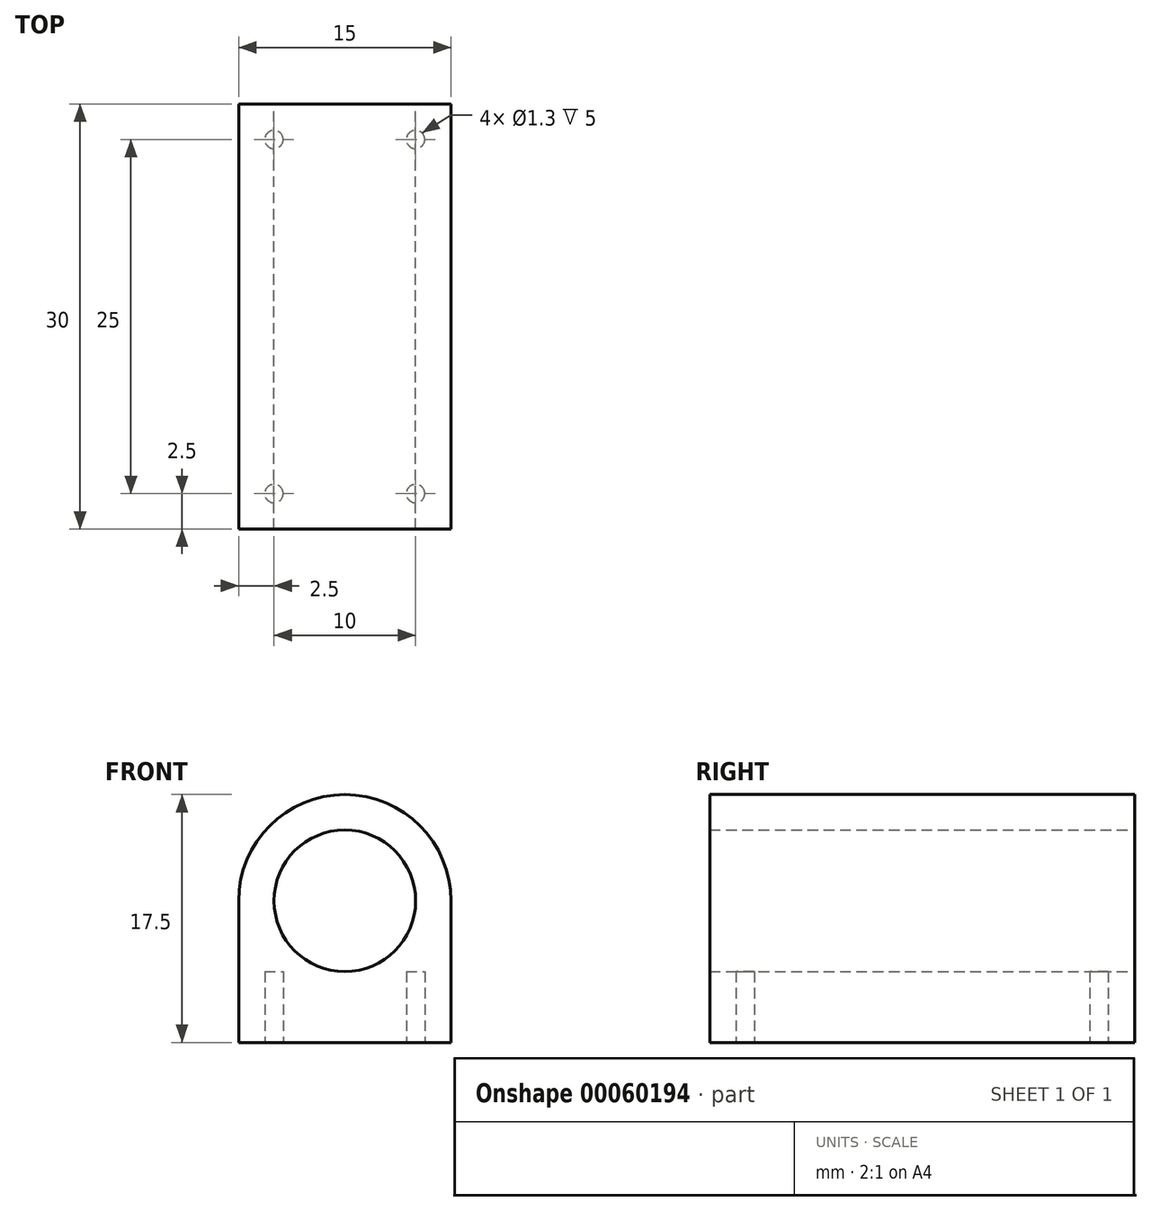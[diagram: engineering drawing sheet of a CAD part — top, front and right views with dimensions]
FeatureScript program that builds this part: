
annotation { "Feature Type Name" : "Feature", "Feature Type Description" : "" }
export const myFeature = defineFeature(function(context is Context, id is Id, definition is map)
    precondition{}
    {
        {
            var Q0;
            Q0=qCreatedBy(makeId("Front.planeOp"),FACE);
            var sketch = newSketch(context, id + "F0", { "sketchPlane" : qUnion([Q0])});
            skLineSegment(sketch, "E0.bottom", {"start": v(-7.5, 0) * mm, "end": v(7.5, 0) * mm});
            skLineSegment(sketch, "E0.left", {"start": v(-7.5, 0) * mm, "end": v(-7.5, 10) * mm});
            skLineSegment(sketch, "E0.right", {"start": v(7.5, 0) * mm, "end": v(7.5, 10) * mm});
            skArc(sketch, "E1", {"start": v(7.5, 10) * mm, "mid": v(0, 17.5) * mm, "end": v(-7.5, 10) * mm});
            skCircle(sketch, "E2", {"center": v(0, 10) * mm, "radius": 5 * mm});
            skSolve(sketch);
        }
        {
            var Q0;
            Q0=makeQuery(id+"F0.imprint","IMPRINT",FACE,{"disambiguationData":[TD([[makeQuery(id+"F0.imprint","IMPRINT",EDGE,{"derivedFrom":sQuery(id+"F0.wireOp",EDGE,"E0.bottom")}),1.0]])]});
            extrude(context, id + "F1", {"entities" : qUnion([Q0]), "depth" : 30 * mm});
        }
        {
            var Q0;
            Q0=makeQuery(id+"F1.opExtrude","SWEPT_FACE",FACE,{"disambiguationData":[OSD([sQuery(id+"F0.wireOp",EDGE,"E0.bottom")])]});
            var sketch = newSketch(context, id + "F2", { "sketchPlane" : qUnion([Q0])});
            skCircle(sketch, "E3", {"center": v(5, 27.5) * mm, "radius": 0.65 * mm});
            skCircle(sketch, "E4", {"center": v(-5, 27.5) * mm, "radius": 0.65 * mm});
            skCircle(sketch, "E5", {"center": v(-5, 2.5) * mm, "radius": 0.65 * mm});
            skCircle(sketch, "E6", {"center": v(5, 2.5) * mm, "radius": 0.65 * mm});
            skSolve(sketch);
        }
        {
            var Q0;
            Q0 = qSketchRegion(id + "F2", true);
            var Q1;
            Q1=makeQuery(id+"F2.imprint","IMPRINT",FACE,{"disambiguationData":[TD([[makeQuery(id+"F2.imprint","IMPRINT",EDGE,{"derivedFrom":sQuery(id+"F2.wireOp",EDGE,"E3")}),1.0]])]});
            extrude(context, id + "F3", {"entities" : qUnion([Q0, Q1]), "operationType" : NewBodyOperationType.REMOVE, "oppositeDirection" : true, "depth" : 5 * mm});
        }
    });
